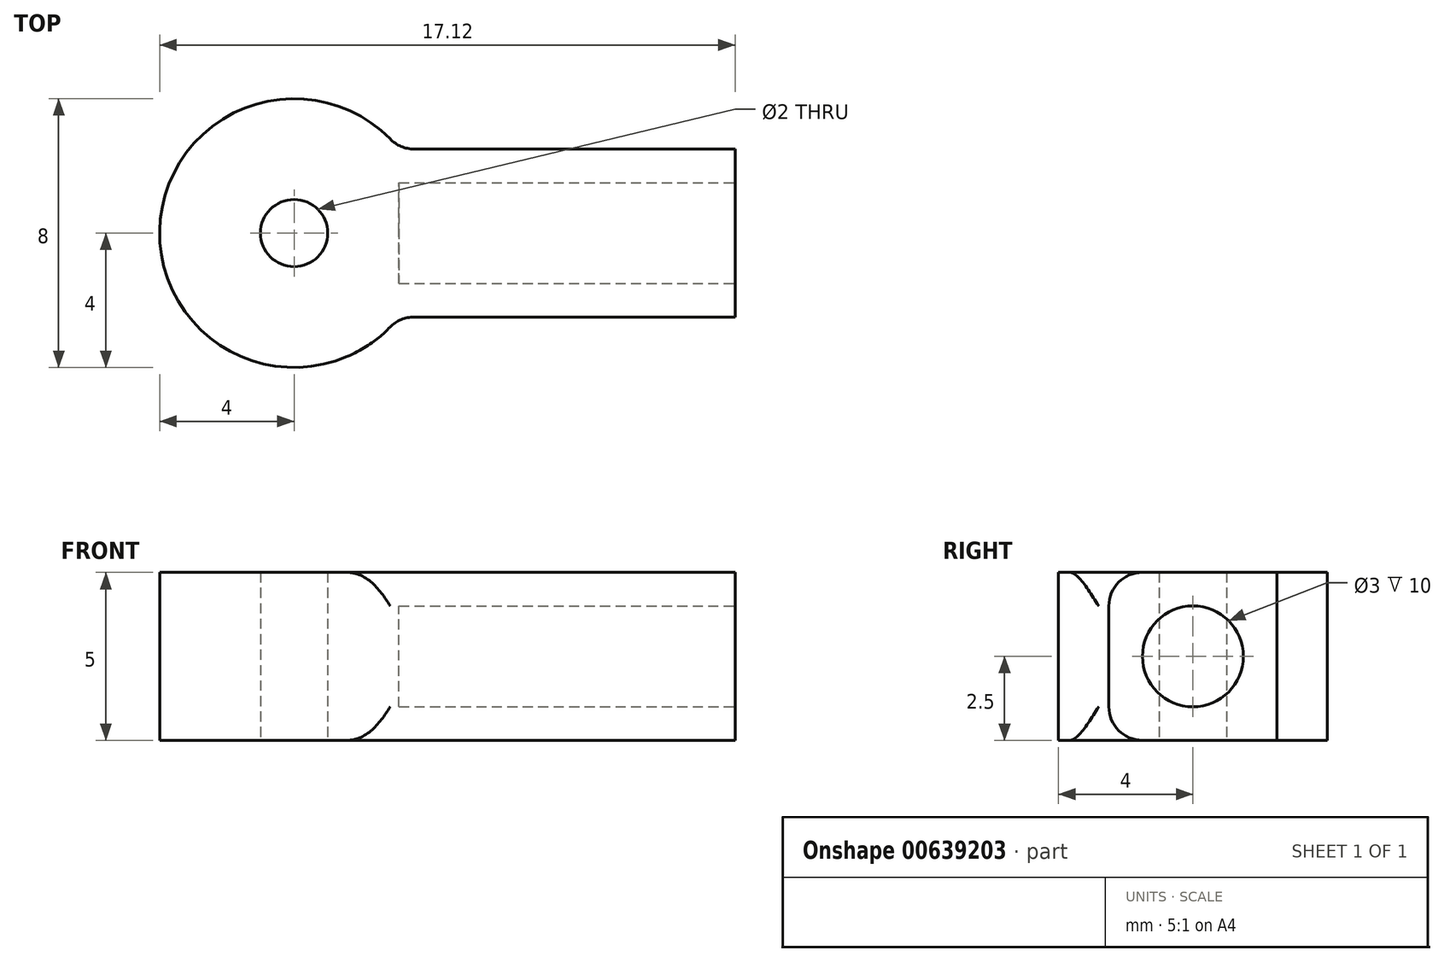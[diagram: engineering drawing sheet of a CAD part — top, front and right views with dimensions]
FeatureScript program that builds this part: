
annotation { "Feature Type Name" : "Feature", "Feature Type Description" : "" }
export const myFeature = defineFeature(function(context is Context, id is Id, definition is map)
    precondition{}
    {
        {
            var Q0;
            Q0=qCreatedBy(makeId("Top.planeOp"),FACE);
            var sketch = newSketch(context, id + "F0", { "sketchPlane" : qUnion([Q0])});
            skCircle(sketch, "E0", {"center": v(0, 0) * mm, "radius": 1 * mm});
            skArc(sketch, "E1.0", {"start": v(3.12, 2.5) * mm, "mid": v(-4, 0) * mm, "end": v(3.12, -2.5) * mm});
            skLineSegment(sketch, "E2", {"start": v(3.12, -2.5) * mm, "end": v(13.12, -2.5) * mm});
            skLineSegment(sketch, "E3", {"start": v(13.12, -2.5) * mm, "end": v(13.12, 2.5) * mm});
            skLineSegment(sketch, "E4", {"start": v(13.12, 2.5) * mm, "end": v(3.12, 2.5) * mm});
            skSolve(sketch);
        }
        {
            var Q0;
            Q0 = qSketchRegion(id + "F0", true);
            extrude(context, id + "F1", {"entities" : qUnion([Q0]), "depth" : 5 * mm, "offsetDistance" : 25 * mm});
        }
        {
            var Q0;
            Q0=makeQuery(id+"F1.opExtrude","SWEPT_FACE",FACE,{"disambiguationData":[OSD([sQuery(id+"F0.wireOp",EDGE,"E3")])]});
            var sketch = newSketch(context, id + "F2", { "sketchPlane" : qUnion([Q0])});
            skCircle(sketch, "E5", {"center": v(0, 2.5) * mm, "radius": 1.5 * mm});
            skLineSegment(sketch, "E6", {"start": v(0, 0) * mm, "end": v(0, 5) * mm, "construction": true});
            skSolve(sketch);
        }
        {
            var Q0;
            Q0 = qSketchRegion(id + "F2", true);
            extrude(context, id + "F3", {"entities" : qUnion([Q0]), "operationType" : NewBodyOperationType.REMOVE, "oppositeDirection" : true, "depth" : 10 * mm, "offsetDistance" : 25 * mm});
        }
        {
            var Q0;
            Q0=makeQuery(id+"F1.opExtrude","SWEPT_EDGE",EDGE,{"disambiguationData":[OSD([sQuery(id+"F0.wireOp",EDGE,"E1.0"),sQuery(id+"F0.wireOp",EDGE,"E4")])]});
            var Q1;
            Q1=makeQuery(id+"F1.opExtrude","SWEPT_EDGE",EDGE,{"disambiguationData":[OSD([sQuery(id+"F0.wireOp",EDGE,"E1.0"),sQuery(id+"F0.wireOp",EDGE,"E2")])]});
            var Q2;
            Q2=makeQuery(id+"F1.opExtrude","CAP_EDGE",EDGE,{"disambiguationData":[OSD([sQuery(id+"F0.wireOp",EDGE,"E2")])],"isStart":false});
            var Q3;
            Q3=makeQuery(id+"F1.opExtrude","CAP_EDGE",EDGE,{"disambiguationData":[OSD([sQuery(id+"F0.wireOp",EDGE,"E2")])],"isStart":true});
            fillet(context, id + "F4", {"entities" : qUnion([Q0, Q1, Q2, Q3]), "radius" : 1 * mm, "tangentPropagation" : true, "allowEdgeOverflow" : false});
        }
    });
